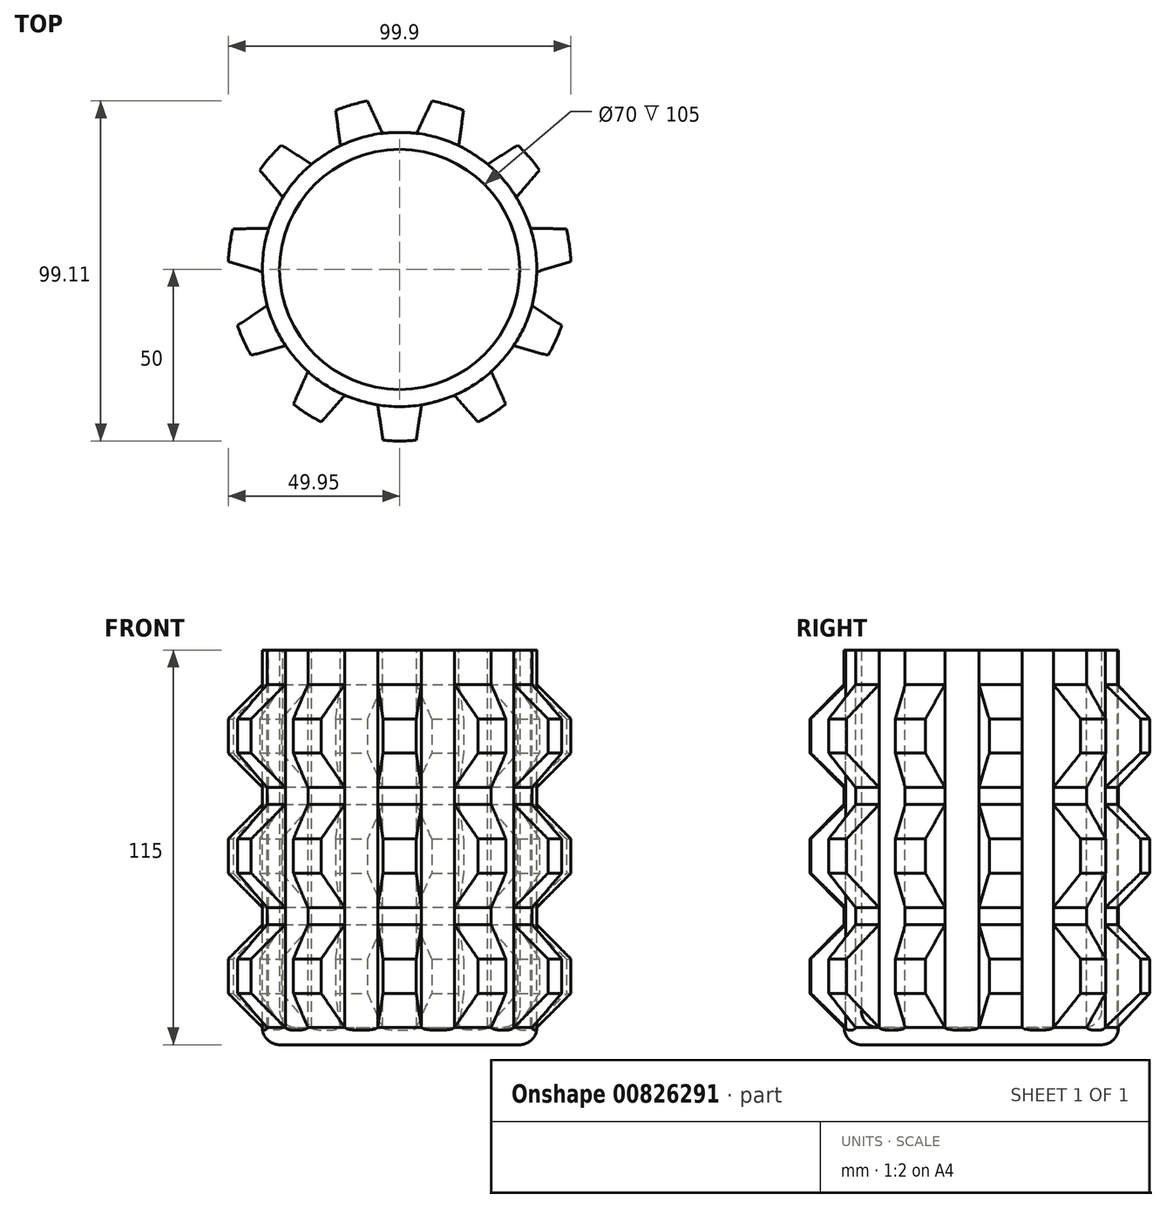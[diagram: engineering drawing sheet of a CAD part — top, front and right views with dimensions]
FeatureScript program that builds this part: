
annotation { "Feature Type Name" : "Feature", "Feature Type Description" : "" }
export const myFeature = defineFeature(function(context is Context, id is Id, definition is map)
    precondition{}
    {
        {
            var Q0;
            Q0=qCreatedBy(makeId("Front.planeOp"),FACE);
            var sketch = newSketch(context, id + "F0", { "sketchPlane" : qUnion([Q0])});
            skLineSegment(sketch, "E0", {"start": v(0, 57.5) * mm, "end": v(0, -57.5) * mm, "construction": true});
            skPoint(sketch, "E1", {"position": v(0, 0) * mm});
            skLineSegment(sketch, "E2", {"start": v(-40, 0) * mm, "end": v(40, 0) * mm, "construction": true});
            skLineSegment(sketch, "E3", {"start": v(-40, -52.5) * mm, "end": v(40, -52.5) * mm, "construction": true});
            skPoint(sketch, "E4", {"position": v(0, -47.5) * mm});
            skLineSegment(sketch, "E5", {"start": v(-40, -57.5) * mm, "end": v(40, -57.5) * mm, "construction": true});
            skPoint(sketch, "E6", {"position": v(0, -57.5) * mm});
            skLineSegment(sketch, "E7", {"start": v(0, 57.5) * mm, "end": v(40, 57.5) * mm, "construction": true});
            skLineSegment(sketch, "E8", {"start": v(40, 57.5) * mm, "end": v(0, 57.5) * mm});
            skLineSegment(sketch, "E9", {"start": v(40, -52.5) * mm, "end": v(40, 57.5) * mm, "construction": true});
            skPoint(sketch, "E10.visualSharp", {"position": v(40, -57.5) * mm});
            skLineSegment(sketch, "E11", {"start": v(40, 57.5) * mm, "end": v(40, -52.5) * mm});
            skLineSegment(sketch, "E12.2", {"start": v(35, 57.5) * mm, "end": v(35, -47.5) * mm});
            skLineSegment(sketch, "E13", {"start": v(0, -52.5) * mm, "end": v(0, 57.5) * mm});
            skLineSegment(sketch, "E14", {"start": v(40, -52.5) * mm, "end": v(40, -52.5) * mm});
            skLineSegment(sketch, "E15", {"start": v(30, -52.5) * mm, "end": v(0, -52.5) * mm});
            skLineSegment(sketch, "E16", {"start": v(35, -57.5) * mm, "end": v(0, -57.5) * mm});
            skLineSegment(sketch, "E17", {"start": v(0, -52.5) * mm, "end": v(0, -57.5) * mm});
            skPoint(sketch, "E18.visualSharp", {"position": v(35, -52.5) * mm});
            skArc(sketch, "E18.filletArc", {"start": v(30, -52.5) * mm, "mid": v(33.54, -51.04) * mm, "end": v(35, -47.5) * mm});
            skArc(sketch, "E19.filletArc", {"start": v(35, -57.5) * mm, "mid": v(38.54, -56.04) * mm, "end": v(40, -52.5) * mm});
            skSolve(sketch);
        }
        {
            var Q0;
            {var subQ1=sQuery(id+"F0.wireOp",EDGE,"E11");Q0=makeQuery(id+"F0.imprint","IMPRINT",FACE,{"disambiguationData":[TD([[makeQuery(id+"F0.imprint","IMPRINT",EDGE,{"derivedFrom":subQ1}),-1.0]])]});}
            var Q1;
            Q1=sQuery(id+"F0.wireOp",EDGE,"E13");
            revolve(context, id + "F1", {"surfaceOperationType" : NewSurfaceOperationType.NEW, "entities" : qUnion([Q0]), "axis" : qUnion([Q1]), "revolveType" : RevolveType.FULL});
        }
        {
            var Q0;
            Q0=qCreatedBy(makeId("Front.planeOp"),FACE);
            var sketch = newSketch(context, id + "F2", { "sketchPlane" : qUnion([Q0])});
            skLineSegment(sketch, "E20.bottom", {"start": v(40, 57.5) * mm, "end": v(-40, 57.5) * mm, "construction": true});
            skPoint(sketch, "E20.middle", {"position": v(0, 0) * mm});
            skPoint(sketch, "E21", {"position": v(0, 57.5) * mm});
            skLineSegment(sketch, "E22", {"start": v(0, 0) * mm, "end": v(0, 57.5) * mm, "construction": true});
            skLineSegment(sketch, "E23", {"start": v(40, 57.5) * mm, "end": v(40, -52.5) * mm, "construction": true});
            skPoint(sketch, "E24", {"position": v(40, 47.5) * mm});
            skLineSegment(sketch, "E25", {"start": v(40, 47.5) * mm, "end": v(50, 37.5) * mm});
            skLineSegment(sketch, "E26", {"start": v(50, 37.5) * mm, "end": v(50, 27.5) * mm});
            skLineSegment(sketch, "E27", {"start": v(50, 27.5) * mm, "end": v(40, 17.5) * mm});
            skLineSegment(sketch, "E28", {"start": v(40, 47.5) * mm, "end": v(40, 17.5) * mm});
            skLineSegment(sketch, "E29.0.1.0", {"start": v(50, 2.5) * mm, "end": v(50, -7.5) * mm});
            skLineSegment(sketch, "E29.0.1.1", {"start": v(40, 12.5) * mm, "end": v(50, 2.5) * mm});
            skLineSegment(sketch, "E29.0.1.2", {"start": v(50, -7.5) * mm, "end": v(40, -17.5) * mm});
            skLineSegment(sketch, "E29.0.1.3", {"start": v(40, 12.5) * mm, "end": v(40, -17.5) * mm});
            skLineSegment(sketch, "E29.0.2.0", {"start": v(50, -32.5) * mm, "end": v(50, -42.5) * mm});
            skLineSegment(sketch, "E29.0.2.1", {"start": v(40, -22.5) * mm, "end": v(50, -32.5) * mm});
            skLineSegment(sketch, "E29.0.2.2", {"start": v(50, -42.5) * mm, "end": v(40, -52.5) * mm});
            skLineSegment(sketch, "E29.0.2.3", {"start": v(40, -22.5) * mm, "end": v(40, -52.5) * mm});
            skLineSegment(sketch, "E29.direction1", {"start": v(50, 27.5) * mm, "end": v(71.7, 27.5) * mm, "construction": true});
            skLineSegment(sketch, "E29.direction2", {"start": v(50, 27.5) * mm, "end": v(50, -7.5) * mm, "construction": true});
            skSolve(sketch);
        }
        {
            var Q0;
            Q0=makeQuery(id+"F2.imprint","IMPRINT",FACE,{"disambiguationData":[TD([[makeQuery(id+"F2.imprint","IMPRINT",EDGE,{"derivedFrom":sQuery(id+"F2.wireOp",EDGE,"E25")}),-1.0]])]});
            var Q1;
            Q1=makeQuery(id+"F2.imprint","IMPRINT",FACE,{"disambiguationData":[TD([[makeQuery(id+"F2.imprint","IMPRINT",EDGE,{"derivedFrom":sQuery(id+"F2.wireOp",EDGE,"E29.0.1.0")}),-1.0]])]});
            var Q2;
            Q2=makeQuery(id+"F2.imprint","IMPRINT",FACE,{"disambiguationData":[TD([[makeQuery(id+"F2.imprint","IMPRINT",EDGE,{"derivedFrom":sQuery(id+"F2.wireOp",EDGE,"E29.0.2.0")}),-1.0]])]});
            var Q3;
            Q3=sQuery(id+"F0.wireOp",EDGE,"E13");
            revolve(context, id + "F3", {"operationType" : NewBodyOperationType.ADD, "surfaceOperationType" : NewSurfaceOperationType.NEW, "entities" : qUnion([Q0, Q1, Q2]), "axis" : qUnion([Q3]), "revolveType" : RevolveType.FULL});
        }
        {
            var Q0;
            Q0=qCreatedBy(makeId("Top.planeOp"),FACE);
            cPlane(context, id + "F4", {"entities" : qUnion([Q0]), "cplaneType" : CPlaneType.OFFSET, "offset" : 140 * mm, "width" : 150 * mm, "height" : 150 * mm});
        }
        {
            var Q0;
            Q0=qCreatedBy(id+"F4.planeOp",FACE);
            var sketch = newSketch(context, id + "F5", { "sketchPlane" : qUnion([Q0])});
            skCircle(sketch, "E30", {"center": v(0, 0) * mm, "radius": 40 * mm, "construction": true});
            skLineSegment(sketch, "E31", {"start": v(0, 0) * mm, "end": v(0, 40) * mm, "construction": true});
            skPoint(sketch, "E32", {"position": v(0, 40) * mm});
            skLineSegment(sketch, "E33", {"start": v(0, 40) * mm, "end": v(0, 54.92) * mm, "construction": true});
            skArc(sketch, "E34", {"start": v(5, 39.69) * mm, "mid": v(0, 39.94) * mm, "end": v(-5, 39.69) * mm});
            skPoint(sketch, "E35.positionSnap0", {"position": v(0, 39.94) * mm});
            skLineSegment(sketch, "E36", {"start": v(5, 39.69) * mm, "end": v(10.08, 50.59) * mm});
            skLineSegment(sketch, "E37", {"start": v(-10.08, 50.59) * mm, "end": v(-5, 39.69) * mm});
            skArc(sketch, "E38", {"start": v(10.08, 50.59) * mm, "mid": v(0, 51.61) * mm, "end": v(-10.08, 50.59) * mm});
            skLineSegment(sketch, "E39.1.0", {"start": v(-35.83, 37.1) * mm, "end": v(-25.66, 30.68) * mm});
            skArc(sketch, "E39.1.1", {"start": v(-18.87, 48) * mm, "mid": v(-27.9, 43.42) * mm, "end": v(-35.83, 37.1) * mm});
            skLineSegment(sketch, "E39.1.2", {"start": v(-17.25, 36.09) * mm, "end": v(-18.87, 48) * mm});
            skArc(sketch, "E39.1.3", {"start": v(-17.25, 36.09) * mm, "mid": v(-21.6, 33.6) * mm, "end": v(-25.66, 30.68) * mm});
            skLineSegment(sketch, "E39.2.0", {"start": v(-50.2, 11.84) * mm, "end": v(-38.18, 11.94) * mm});
            skArc(sketch, "E39.2.1", {"start": v(-41.83, 30.19) * mm, "mid": v(-46.95, 21.44) * mm, "end": v(-50.2, 11.84) * mm});
            skLineSegment(sketch, "E39.2.2", {"start": v(-34.02, 21.03) * mm, "end": v(-41.83, 30.19) * mm});
            skArc(sketch, "E39.2.3", {"start": v(-34.02, 21.03) * mm, "mid": v(-36.33, 16.6) * mm, "end": v(-38.18, 11.94) * mm});
            skLineSegment(sketch, "E39.3.0", {"start": v(-48.64, -17.18) * mm, "end": v(-38.57, -10.6) * mm});
            skArc(sketch, "E39.3.1", {"start": v(-51.5, 2.78) * mm, "mid": v(-51.09, -7.35) * mm, "end": v(-48.64, -17.18) * mm});
            skLineSegment(sketch, "E39.3.2", {"start": v(-40, -0.7) * mm, "end": v(-51.5, 2.78) * mm});
            skArc(sketch, "E39.3.3", {"start": v(-40, -0.7) * mm, "mid": v(-39.53, -5.68) * mm, "end": v(-38.57, -10.6) * mm});
            skLineSegment(sketch, "E39.4.0", {"start": v(-31.63, -40.75) * mm, "end": v(-26.72, -29.77) * mm});
            skArc(sketch, "E39.4.1", {"start": v(-44.83, -25.5) * mm, "mid": v(-39, -33.8) * mm, "end": v(-31.63, -40.75) * mm});
            skLineSegment(sketch, "E39.4.2", {"start": v(-33.27, -22.21) * mm, "end": v(-44.83, -25.5) * mm});
            skArc(sketch, "E39.4.3", {"start": v(-33.27, -22.21) * mm, "mid": v(-30.18, -26.15) * mm, "end": v(-26.72, -29.77) * mm});
            skLineSegment(sketch, "E39.5.0", {"start": v(-4.58, -51.38) * mm, "end": v(-6.38, -39.49) * mm});
            skArc(sketch, "E39.5.1", {"start": v(-23.93, -45.7) * mm, "mid": v(-14.54, -49.52) * mm, "end": v(-4.58, -51.38) * mm});
            skLineSegment(sketch, "E39.5.2", {"start": v(-15.98, -36.67) * mm, "end": v(-23.93, -45.7) * mm});
            skArc(sketch, "E39.5.3", {"start": v(-15.98, -36.67) * mm, "mid": v(-11.25, -38.32) * mm, "end": v(-6.38, -39.49) * mm});
            skLineSegment(sketch, "E39.6.0", {"start": v(23.93, -45.7) * mm, "end": v(15.98, -36.67) * mm});
            skArc(sketch, "E39.6.1", {"start": v(4.58, -51.38) * mm, "mid": v(14.54, -49.52) * mm, "end": v(23.93, -45.7) * mm});
            skLineSegment(sketch, "E39.6.2", {"start": v(6.38, -39.49) * mm, "end": v(4.58, -51.38) * mm});
            skArc(sketch, "E39.6.3", {"start": v(6.38, -39.49) * mm, "mid": v(11.25, -38.32) * mm, "end": v(15.98, -36.67) * mm});
            skLineSegment(sketch, "E39.7.0", {"start": v(44.83, -25.5) * mm, "end": v(33.27, -22.21) * mm});
            skArc(sketch, "E39.7.1", {"start": v(31.63, -40.75) * mm, "mid": v(39, -33.8) * mm, "end": v(44.83, -25.5) * mm});
            skLineSegment(sketch, "E39.7.2", {"start": v(26.72, -29.77) * mm, "end": v(31.63, -40.75) * mm});
            skArc(sketch, "E39.7.3", {"start": v(26.72, -29.77) * mm, "mid": v(30.18, -26.15) * mm, "end": v(33.27, -22.21) * mm});
            skLineSegment(sketch, "E39.8.0", {"start": v(51.5, 2.78) * mm, "end": v(40, -0.7) * mm});
            skArc(sketch, "E39.8.1", {"start": v(48.64, -17.18) * mm, "mid": v(51.09, -7.35) * mm, "end": v(51.5, 2.78) * mm});
            skLineSegment(sketch, "E39.8.2", {"start": v(38.57, -10.6) * mm, "end": v(48.64, -17.18) * mm});
            skArc(sketch, "E39.8.3", {"start": v(38.57, -10.6) * mm, "mid": v(39.53, -5.68) * mm, "end": v(40, -0.7) * mm});
            skLineSegment(sketch, "E39.9.0", {"start": v(41.83, 30.19) * mm, "end": v(34.02, 21.03) * mm});
            skArc(sketch, "E39.9.1", {"start": v(50.2, 11.84) * mm, "mid": v(46.95, 21.44) * mm, "end": v(41.83, 30.19) * mm});
            skLineSegment(sketch, "E39.9.2", {"start": v(38.18, 11.94) * mm, "end": v(50.2, 11.84) * mm});
            skArc(sketch, "E39.9.3", {"start": v(38.18, 11.94) * mm, "mid": v(36.33, 16.6) * mm, "end": v(34.02, 21.03) * mm});
            skLineSegment(sketch, "E40.2.10.0", {"start": v(18.87, 48) * mm, "end": v(17.25, 36.09) * mm});
            skArc(sketch, "E40.3.10.0", {"start": v(35.83, 37.1) * mm, "mid": v(27.9, 43.42) * mm, "end": v(18.87, 48) * mm});
            skLineSegment(sketch, "E40.7.10.0", {"start": v(25.66, 30.68) * mm, "end": v(35.83, 37.1) * mm});
            skArc(sketch, "E40.10.10.0", {"start": v(25.66, 30.68) * mm, "mid": v(21.6, 33.6) * mm, "end": v(17.25, 36.09) * mm});
            skSolve(sketch);
        }
        {
            var Q0;
            Q0=makeQuery(id+"F5.imprint","IMPRINT",FACE,{"disambiguationData":[TD([[makeQuery(id+"F5.imprint","IMPRINT",EDGE,{"derivedFrom":sQuery(id+"F5.wireOp",EDGE,"E39.1.0")}),1.0]])]});
            var Q1;
            Q1=makeQuery(id+"F5.imprint","IMPRINT",FACE,{"disambiguationData":[TD([[makeQuery(id+"F5.imprint","IMPRINT",EDGE,{"derivedFrom":sQuery(id+"F5.wireOp",EDGE,"E34")}),-1.0]])]});
            var Q2;
            Q2=makeQuery(id+"F5.imprint","IMPRINT",FACE,{"disambiguationData":[TD([[makeQuery(id+"F5.imprint","IMPRINT",EDGE,{"derivedFrom":sQuery(id+"F5.wireOp",EDGE,"E39.12.0")}),1.0]])]});
            var Q3;
            Q3=makeQuery(id+"F5.imprint","IMPRINT",FACE,{"disambiguationData":[TD([[makeQuery(id+"F5.imprint","IMPRINT",EDGE,{"derivedFrom":sQuery(id+"F5.wireOp",EDGE,"E39.2.0")}),1.0]])]});
            var Q4;
            Q4=makeQuery(id+"F5.imprint","IMPRINT",FACE,{"disambiguationData":[TD([[makeQuery(id+"F5.imprint","IMPRINT",EDGE,{"derivedFrom":sQuery(id+"F5.wireOp",EDGE,"E39.3.0")}),1.0]])]});
            var Q5;
            Q5=makeQuery(id+"F5.imprint","IMPRINT",FACE,{"disambiguationData":[TD([[makeQuery(id+"F5.imprint","IMPRINT",EDGE,{"derivedFrom":sQuery(id+"F5.wireOp",EDGE,"E39.4.0")}),1.0]])]});
            var Q6;
            Q6=makeQuery(id+"F5.imprint","IMPRINT",FACE,{"disambiguationData":[TD([[makeQuery(id+"F5.imprint","IMPRINT",EDGE,{"derivedFrom":sQuery(id+"F5.wireOp",EDGE,"E39.5.0")}),1.0]])]});
            var Q7;
            Q7=makeQuery(id+"F5.imprint","IMPRINT",FACE,{"disambiguationData":[TD([[makeQuery(id+"F5.imprint","IMPRINT",EDGE,{"derivedFrom":sQuery(id+"F5.wireOp",EDGE,"E39.6.0")}),1.0]])]});
            var Q8;
            Q8=makeQuery(id+"F5.imprint","IMPRINT",FACE,{"disambiguationData":[TD([[makeQuery(id+"F5.imprint","IMPRINT",EDGE,{"derivedFrom":sQuery(id+"F5.wireOp",EDGE,"E39.7.0")}),1.0]])]});
            var Q9;
            Q9=makeQuery(id+"F5.imprint","IMPRINT",FACE,{"disambiguationData":[TD([[makeQuery(id+"F5.imprint","IMPRINT",EDGE,{"derivedFrom":sQuery(id+"F5.wireOp",EDGE,"E39.8.0")}),1.0]])]});
            var Q10;
            Q10=makeQuery(id+"F5.imprint","IMPRINT",FACE,{"disambiguationData":[TD([[makeQuery(id+"F5.imprint","IMPRINT",EDGE,{"derivedFrom":sQuery(id+"F5.wireOp",EDGE,"E39.9.0")}),1.0]])]});
            var Q11;
            Q11=makeQuery(id+"F5.imprint","IMPRINT",FACE,{"disambiguationData":[TD([[makeQuery(id+"F5.imprint","IMPRINT",EDGE,{"derivedFrom":sQuery(id+"F5.wireOp",EDGE,"E39.10.0")}),1.0]])]});
            var Q12;
            Q12=makeQuery(id+"F5.imprint","IMPRINT",FACE,{"disambiguationData":[TD([[makeQuery(id+"F5.imprint","IMPRINT",EDGE,{"derivedFrom":sQuery(id+"F5.wireOp",EDGE,"E39.11.0")}),1.0]])]});
            var Q13;
            Q13=makeQuery(id+"F5.imprint","IMPRINT",FACE,{"disambiguationData":[TD([[makeQuery(id+"F5.imprint","IMPRINT",EDGE,{"derivedFrom":sQuery(id+"F5.wireOp",EDGE,"E40.2.10.0")}),1.0]])]});
            extrude(context, id + "F6", {"entities" : qUnion([Q0, Q1, Q2, Q3, Q4, Q5, Q6, Q7, Q8, Q9, Q10, Q11, Q12, Q13]), "operationType" : NewBodyOperationType.REMOVE, "endBound" : BoundingType.THROUGH_ALL, "oppositeDirection" : true, "depth" : 25 * mm, "offsetDistance" : 25 * mm});
        }
    });
